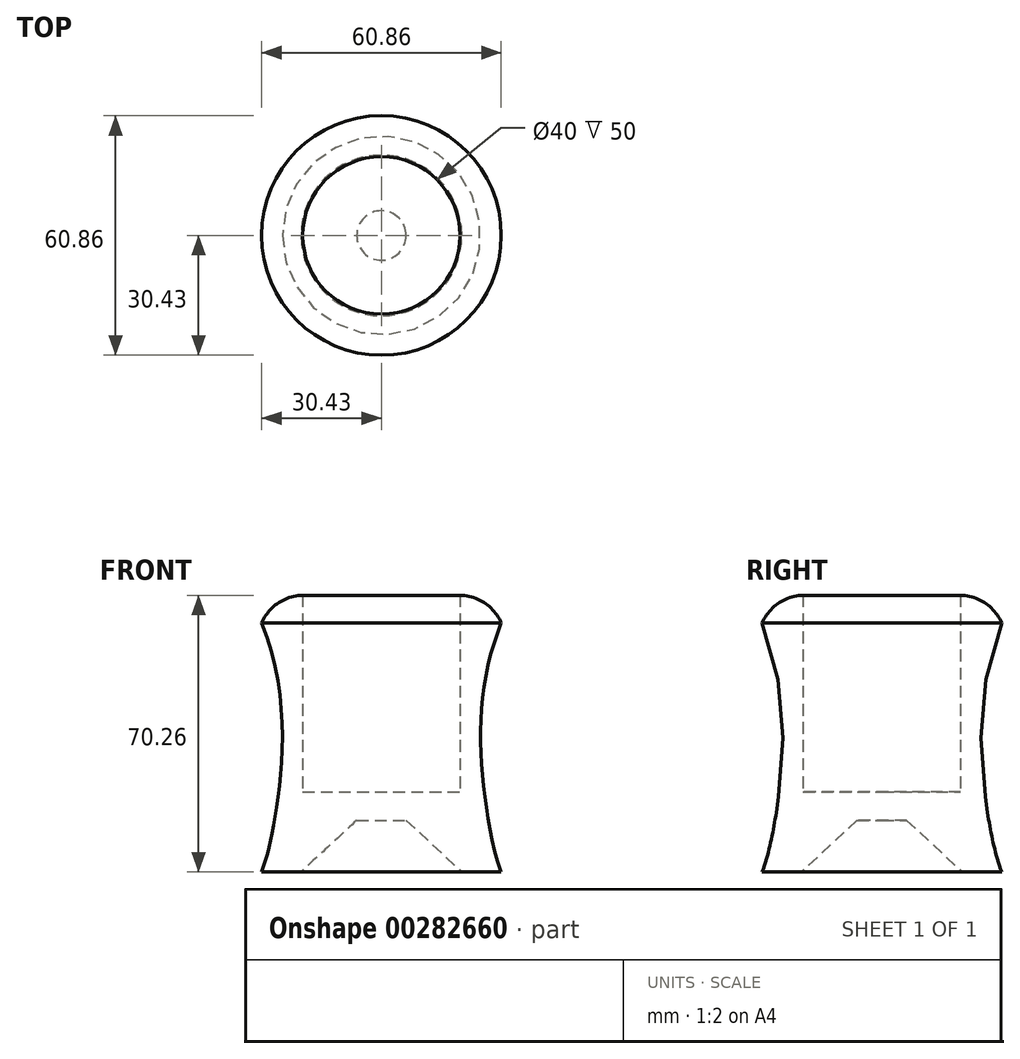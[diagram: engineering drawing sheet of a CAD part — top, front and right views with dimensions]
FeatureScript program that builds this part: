
annotation { "Feature Type Name" : "Feature", "Feature Type Description" : "" }
export const myFeature = defineFeature(function(context is Context, id is Id, definition is map)
    precondition{}
    {
        {
            var Q0;
            Q0=qCreatedBy(makeId("Front.planeOp"),FACE);
            var sketch = newSketch(context, id + "F0", { "sketchPlane" : qUnion([Q0])});
            skLineSegment(sketch, "E0", {"start": v(0, 0) * mm, "end": v(-20, 0) * mm});
            skLineSegment(sketch, "E1", {"start": v(-20, 0) * mm, "end": v(-20, 50) * mm});
            skLineSegment(sketch, "E2", {"start": v(0, 0) * mm, "end": v(0, 112.09) * mm, "construction": true});
            skArc(sketch, "E3", {"start": v(-20, 50) * mm, "mid": v(-26.26, 48) * mm, "end": v(-30.43, 42.92) * mm});
            skFitSpline(sketch, "E4", {"points": [v(-30.43, 42.92) * mm, v(-26.94, -5.84) * mm, v(-30.43, -20.26) * mm], "startDerivative": vector(34.47, -83.38) * mm, "endDerivative": vector(-12.53, -34.38) * mm});
            skLineSegment(sketch, "E5", {"start": v(-30.43, -20.26) * mm, "end": v(-20.41, -20.26) * mm});
            skLineSegment(sketch, "E6", {"start": v(-20.41, -20.26) * mm, "end": v(-6.28, -7.15) * mm});
            skLineSegment(sketch, "E7", {"start": v(-6.28, -7.15) * mm, "end": v(0, -7.15) * mm});
            skPoint(sketch, "E8", {"position": v(-20, 25) * mm});
            skLineSegment(sketch, "E9", {"start": v(0, -7.15) * mm, "end": v(0, 0) * mm});
            skSolve(sketch);
        }
        {
            var Q0;
            Q0 = qSketchRegion(id + "F0", true);
            var Q1;
            Q1=sQuery(id+"F0.wireOp",EDGE,"E2");
            revolve(context, id + "F1", {"entities" : qUnion([Q0]), "axis" : qUnion([Q1]), "revolveType" : RevolveType.FULL});
        }
    });
